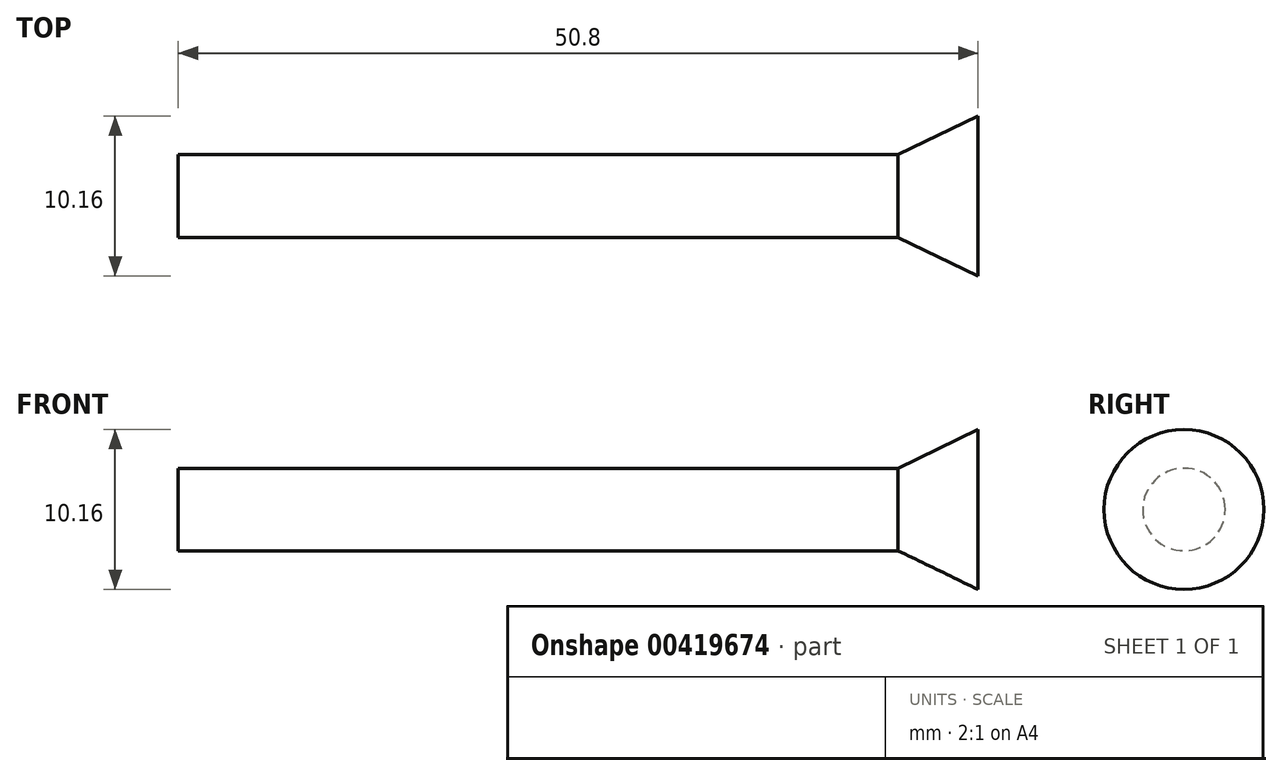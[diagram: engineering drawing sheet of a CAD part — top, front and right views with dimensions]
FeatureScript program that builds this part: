
annotation { "Feature Type Name" : "Feature", "Feature Type Description" : "" }
export const myFeature = defineFeature(function(context is Context, id is Id, definition is map)
    precondition{}
    {
        {
            var Q0;
            Q0=qCreatedBy(makeId("Right.planeOp"),FACE);
            var sketch = newSketch(context, id + "F0", { "sketchPlane" : qUnion([Q0])});
            skCircle(sketch, "E0", {"center": v(0, 0) * mm, "radius": 2.62 * mm});
            skSolve(sketch);
        }
        {
            var Q0;
            Q0=qSketchRegion(id+"F0",true);
            extrude(context, id + "F1", {"entities" : qUnion([Q0]), "depth" : 45.72 * mm, "offsetDistance" : 25.4 * mm});
        }
        {
            var Q0;
            Q0=qCreatedBy(makeId("Front.planeOp"),FACE);
            var sketch = newSketch(context, id + "F2", { "sketchPlane" : qUnion([Q0])});
            skLineSegment(sketch, "E1.0", {"start": v(45.72, 2.62) * mm, "end": v(45.72, -2.62) * mm});
            skLineSegment(sketch, "E2", {"start": v(45.72, 2.62) * mm, "end": v(50.8, 5.08) * mm});
            skLineSegment(sketch, "E3", {"start": v(50.8, 5.08) * mm, "end": v(50.8, 0) * mm});
            skLineSegment(sketch, "E4", {"start": v(50.8, 0) * mm, "end": v(45.72, 0) * mm});
            skLineSegment(sketch, "E5", {"start": v(45.72, 0) * mm, "end": v(45.72, 2.62) * mm});
            skSolve(sketch);
        }
        {
            var Q0;
            Q0=makeQuery(id+"F2.imprint","IMPRINT",FACE,{"disambiguationData":[TD([[makeQuery(id+"F2.imprint","IMPRINT",EDGE,{"derivedFrom":sQuery(id+"F2.wireOp",EDGE,"E2")}),-1.0]])]});
            var Q1;
            Q1=sQuery(id+"F2.wireOp",EDGE,"E4");
            revolve(context, id + "F3", {"operationType" : NewBodyOperationType.ADD, "entities" : qUnion([Q0]), "axis" : qUnion([Q1]), "revolveType" : RevolveType.FULL});
        }
    });
